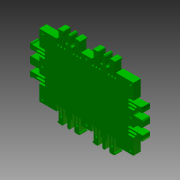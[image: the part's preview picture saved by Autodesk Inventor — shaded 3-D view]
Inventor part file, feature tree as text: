
AUTODESK INVENTOR PART (.ipt)
format: ipt  version: 2012 SP1 (Build 160190100, 190)  size: 510,464 bytes
history: native  units: in
note: dims shown in document units (in); Inventor stores cm internally (conversion verified against a paired STEP export)
features: other x4, extrude x2
ambient origin geometry x8: Origin, YZ Plane, XZ Plane, XY Plane, X Axis, Y Axis, Z Axis, Center Point
bodies: Solid1 (feature_tree)
feature tree (6):
  other  "skeleton.ipt"
  other  "DRILL-THROUGH"
  other  "STOCK_12MM"
  extrude  "Extrusion1"  Depth=0.3937in
  extrude  "Extrusion2"  Depth=0.4724in
  other  "THROUGH-CUT"
